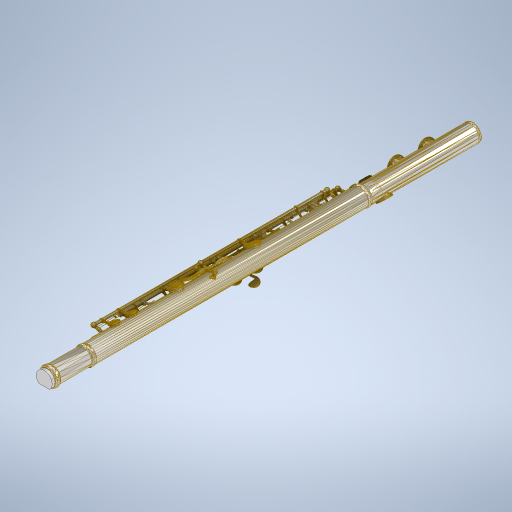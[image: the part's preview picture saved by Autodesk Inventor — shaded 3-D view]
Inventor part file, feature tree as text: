
AUTODESK INVENTOR PART (.ipt)
format: ipt  version: 2024 (Build 280153000, 153)  size: 59,981,824 bytes
history: native  units: in
note: dims shown in document units (in); Inventor stores cm internally (conversion verified against a paired STEP export)
features: other x3, plane x3, extrude x2, projected_geometry x1
ambient origin geometry x8: Origin, YZ Plane, XZ Plane, XY Plane, X Axis, Y Axis, Z Axis, Center Point
bodies: Solid1 (feature_tree)
feature tree (9):
  other  "resto_flauta"
  plane  "Work Plane1"
  extrude  "Extrusion1"  Depth=0.1in TaperAngle=0.0deg
  plane  "Work Plane3"
  extrude  "Extrusion2"  Depth=0.1in TaperAngle=0.0deg
  plane  "Work Plane4"
  projected_geometry  "Projected Loop1"
  other  "MeshFeature1"
  other  "Srf1"
